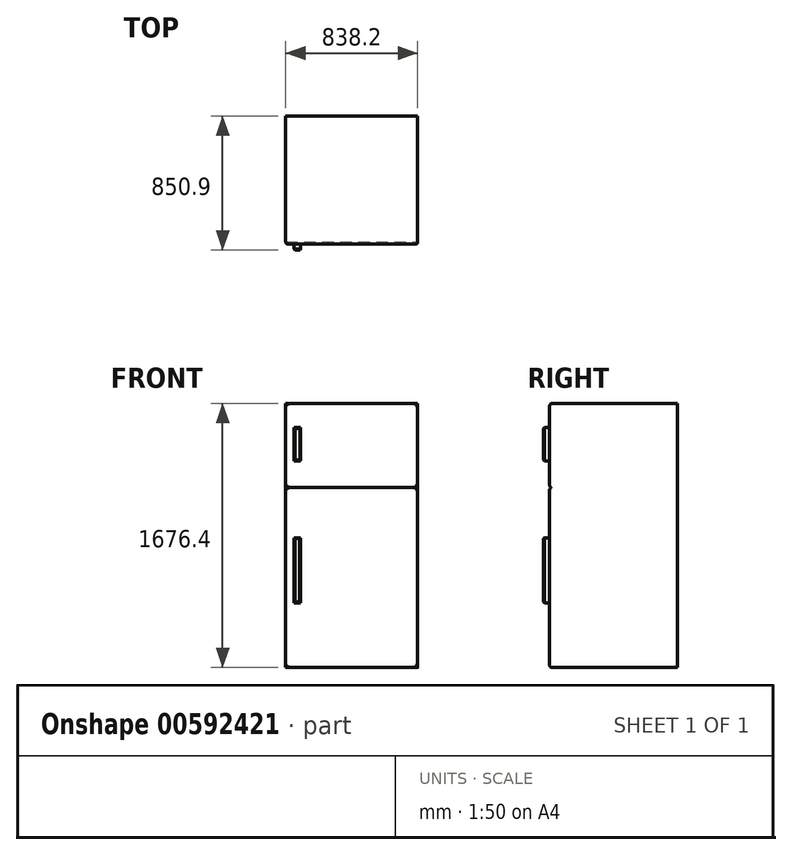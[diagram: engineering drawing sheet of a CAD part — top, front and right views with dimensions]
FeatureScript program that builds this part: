
annotation { "Feature Type Name" : "Feature", "Feature Type Description" : "" }
export const myFeature = defineFeature(function(context is Context, id is Id, definition is map)
    precondition{}
    {
        {
            var Q0;
            Q0=qCreatedBy(makeId("Top.planeOp"),FACE);
            var sketch = newSketch(context, id + "F0", { "sketchPlane" : qUnion([Q0])});
            skLineSegment(sketch, "E0.bottom", {"start": v(419.1, -381) * mm, "end": v(-419.1, -381) * mm});
            skLineSegment(sketch, "E0.top", {"start": v(419.1, 381) * mm, "end": v(-419.1, 381) * mm});
            skLineSegment(sketch, "E0.left", {"start": v(419.1, -381) * mm, "end": v(419.1, 381) * mm});
            skLineSegment(sketch, "E0.right", {"start": v(-419.1, -381) * mm, "end": v(-419.1, 381) * mm});
            skPoint(sketch, "E0.middle", {"position": v(0, 0) * mm});
            skSolve(sketch);
        }
        {
            var Q0;
            Q0=makeQuery(id+"F0.imprint","IMPRINT",FACE,{"disambiguationData":[TD([[makeQuery(id+"F0.imprint","IMPRINT",EDGE,{"derivedFrom":sQuery(id+"F0.wireOp",EDGE,"E0.bottom")}),-1.0]])]});
            extrude(context, id + "F1", {"entities" : qUnion([Q0]), "depth" : 1676.4 * mm, "offsetDistance" : 25.4 * mm});
        }
        {
            var Q0;
            Q0=makeQuery(id+"F1.opExtrude","SWEPT_FACE",FACE,{"disambiguationData":[OSD([sQuery(id+"F0.wireOp",EDGE,"E0.bottom")])]});
            var sketch = newSketch(context, id + "F2", { "sketchPlane" : qUnion([Q0])});
            skLineSegment(sketch, "E1.bottom", {"start": v(-419.1, 1676.4) * mm, "end": v(419.1, 1676.4) * mm});
            skLineSegment(sketch, "E1.top", {"start": v(-419.1, 1143) * mm, "end": v(419.1, 1143) * mm});
            skLineSegment(sketch, "E1.left", {"start": v(-419.1, 1676.4) * mm, "end": v(-419.1, 1143) * mm});
            skLineSegment(sketch, "E1.right", {"start": v(419.1, 1676.4) * mm, "end": v(419.1, 1143) * mm});
            skLineSegment(sketch, "E2.bottom", {"start": v(-365.33, 1516.68) * mm, "end": v(-327.23, 1516.68) * mm});
            skLineSegment(sketch, "E2.top", {"start": v(-365.33, 1313.48) * mm, "end": v(-327.23, 1313.48) * mm});
            skLineSegment(sketch, "E2.left", {"start": v(-365.33, 1516.68) * mm, "end": v(-365.33, 1313.48) * mm});
            skLineSegment(sketch, "E2.right", {"start": v(-327.23, 1516.68) * mm, "end": v(-327.23, 1313.48) * mm});
            skLineSegment(sketch, "E3.bottom", {"start": v(-365.33, 822.07) * mm, "end": v(-327.23, 822.07) * mm});
            skLineSegment(sketch, "E3.top", {"start": v(-365.33, 415.67) * mm, "end": v(-327.23, 415.67) * mm});
            skLineSegment(sketch, "E3.left", {"start": v(-365.33, 822.07) * mm, "end": v(-365.33, 415.67) * mm});
            skLineSegment(sketch, "E3.right", {"start": v(-327.23, 822.07) * mm, "end": v(-327.23, 415.67) * mm});
            skSolve(sketch);
        }
        {
            var Q0;
            Q0=makeQuery(id+"F2.imprint","IMPRINT",FACE,{"disambiguationData":[TD([[makeQuery(id+"F2.imprint","IMPRINT",EDGE,{"derivedFrom":sQuery(id+"F2.wireOp",EDGE,"E1.bottom")}),1.0]])]});
            var Q1;
            Q1=makeQuery(id+"F2.imprint","IMPRINT",FACE,{"disambiguationData":[TD([[makeQuery(id+"F2.imprint","IMPRINT",EDGE,{"derivedFrom":sQuery(id+"F2.wireOp",EDGE,"E2.bottom")}),-1.0]])]});
            extrude(context, id + "F3", {"entities" : qUnion([Q0, Q1]), "operationType" : NewBodyOperationType.ADD, "depth" : 50.8 * mm, "offsetDistance" : 25.4 * mm});
        }
        {
            var Q0;
            Q0=makeQuery(id+"F3.opExtrude","CAP_FACE",FACE,{"disambiguationData":[OSD([sQuery(id+"F2.wireOp",EDGE,"E1.bottom"),sQuery(id+"F2.wireOp",EDGE,"E1.top"),sQuery(id+"F2.wireOp",EDGE,"E1.left"),sQuery(id+"F2.wireOp",EDGE,"E1.right")])],"isStart":false});
            fillet(context, id + "F4", {"entities" : qUnion([Q0]), "radius" : 12.7 * mm, "tangentPropagation" : true, "allowEdgeOverflow" : false});
        }
        {
            var Q0;
            Q0=makeQuery(id+"F1.opExtrude","SWEPT_FACE",FACE,{"disambiguationData":[OSD([sQuery(id+"F0.wireOp",EDGE,"E0.bottom")])]});
            extrude(context, id + "F5", {"entities" : qUnion([Q0]), "operationType" : NewBodyOperationType.ADD, "depth" : 50.8 * mm, "offsetDistance" : 25.4 * mm});
        }
        {
            var Q0;
            Q0=makeQuery(id+"F5.opExtrude","CAP_FACE",FACE,{"disambiguationData":[OSD([sQuery(id+"F0.wireOp",EDGE,"E0.bottom")])],"isStart":false});
            fillet(context, id + "F6", {"entities" : qUnion([Q0]), "radius" : 12.7 * mm, "tangentPropagation" : true, "allowEdgeOverflow" : false});
        }
        {
            var Q0;
            Q0=makeQuery(id+"F3.opExtrude","CAP_FACE",FACE,{"disambiguationData":[OSD([sQuery(id+"F2.wireOp",EDGE,"E1.bottom"),sQuery(id+"F2.wireOp",EDGE,"E1.top"),sQuery(id+"F2.wireOp",EDGE,"E1.left"),sQuery(id+"F2.wireOp",EDGE,"E1.right")])],"isStart":false});
            var sketch = newSketch(context, id + "F7", { "sketchPlane" : qUnion([Q0])});
            skLineSegment(sketch, "E4.bottom", {"start": v(-365.48, 1524.32) * mm, "end": v(-324.8, 1524.32) * mm});
            skLineSegment(sketch, "E4.top", {"start": v(-365.48, 1312.07) * mm, "end": v(-324.8, 1312.07) * mm});
            skLineSegment(sketch, "E4.left", {"start": v(-365.48, 1524.32) * mm, "end": v(-365.48, 1312.07) * mm});
            skLineSegment(sketch, "E4.right", {"start": v(-324.8, 1524.32) * mm, "end": v(-324.8, 1312.07) * mm});
            skSolve(sketch);
        }
        {
            var Q0;
            Q0=makeQuery(id+"F7.imprint","IMPRINT",FACE,{"disambiguationData":[TD([[makeQuery(id+"F7.imprint","IMPRINT",EDGE,{"derivedFrom":sQuery(id+"F7.wireOp",EDGE,"E4.bottom")}),-1.0]])]});
            extrude(context, id + "F8", {"entities" : qUnion([Q0]), "operationType" : NewBodyOperationType.ADD, "depth" : 38.1 * mm, "offsetDistance" : 25.4 * mm});
        }
        {
            var Q0;
            Q0=makeQuery(id+"F8.opExtrude","CAP_FACE",FACE,{"disambiguationData":[OSD([sQuery(id+"F7.wireOp",EDGE,"E4.bottom"),sQuery(id+"F7.wireOp",EDGE,"E4.top"),sQuery(id+"F7.wireOp",EDGE,"E4.left"),sQuery(id+"F7.wireOp",EDGE,"E4.right")])],"isStart":false});
            chamfer(context, id + "F9", {"entities" : qUnion([Q0]), "width" : 5.08 * mm, "tangentPropagation" : true});
        }
        {
            var Q0;
            Q0=makeQuery(id+"F5.opExtrude","CAP_FACE",FACE,{"disambiguationData":[OSD([sQuery(id+"F0.wireOp",EDGE,"E0.bottom")])],"isStart":false});
            var sketch = newSketch(context, id + "F10", { "sketchPlane" : qUnion([Q0])});
            skLineSegment(sketch, "E5.bottom", {"start": v(-365.48, 823.88) * mm, "end": v(-326.57, 823.88) * mm});
            skLineSegment(sketch, "E5.top", {"start": v(-365.48, 409.98) * mm, "end": v(-326.57, 409.98) * mm});
            skLineSegment(sketch, "E5.left", {"start": v(-365.48, 823.88) * mm, "end": v(-365.48, 409.98) * mm});
            skLineSegment(sketch, "E5.right", {"start": v(-326.57, 823.88) * mm, "end": v(-326.57, 409.98) * mm});
            skSolve(sketch);
        }
        {
            var Q0;
            Q0=makeQuery(id+"F10.imprint","IMPRINT",FACE,{"disambiguationData":[TD([[makeQuery(id+"F10.imprint","IMPRINT",EDGE,{"derivedFrom":sQuery(id+"F10.wireOp",EDGE,"E5.bottom")}),-1.0]])]});
            extrude(context, id + "F11", {"entities" : qUnion([Q0]), "operationType" : NewBodyOperationType.ADD, "depth" : 38.1 * mm, "offsetDistance" : 25.4 * mm});
        }
        {
            var Q0;
            Q0=makeQuery(id+"F11.opExtrude","CAP_FACE",FACE,{"disambiguationData":[OSD([sQuery(id+"F10.wireOp",EDGE,"E5.bottom"),sQuery(id+"F10.wireOp",EDGE,"E5.top"),sQuery(id+"F10.wireOp",EDGE,"E5.left"),sQuery(id+"F10.wireOp",EDGE,"E5.right")])],"isStart":false});
            chamfer(context, id + "F12", {"entities" : qUnion([Q0]), "width" : 5.08 * mm, "tangentPropagation" : true});
        }
    });
